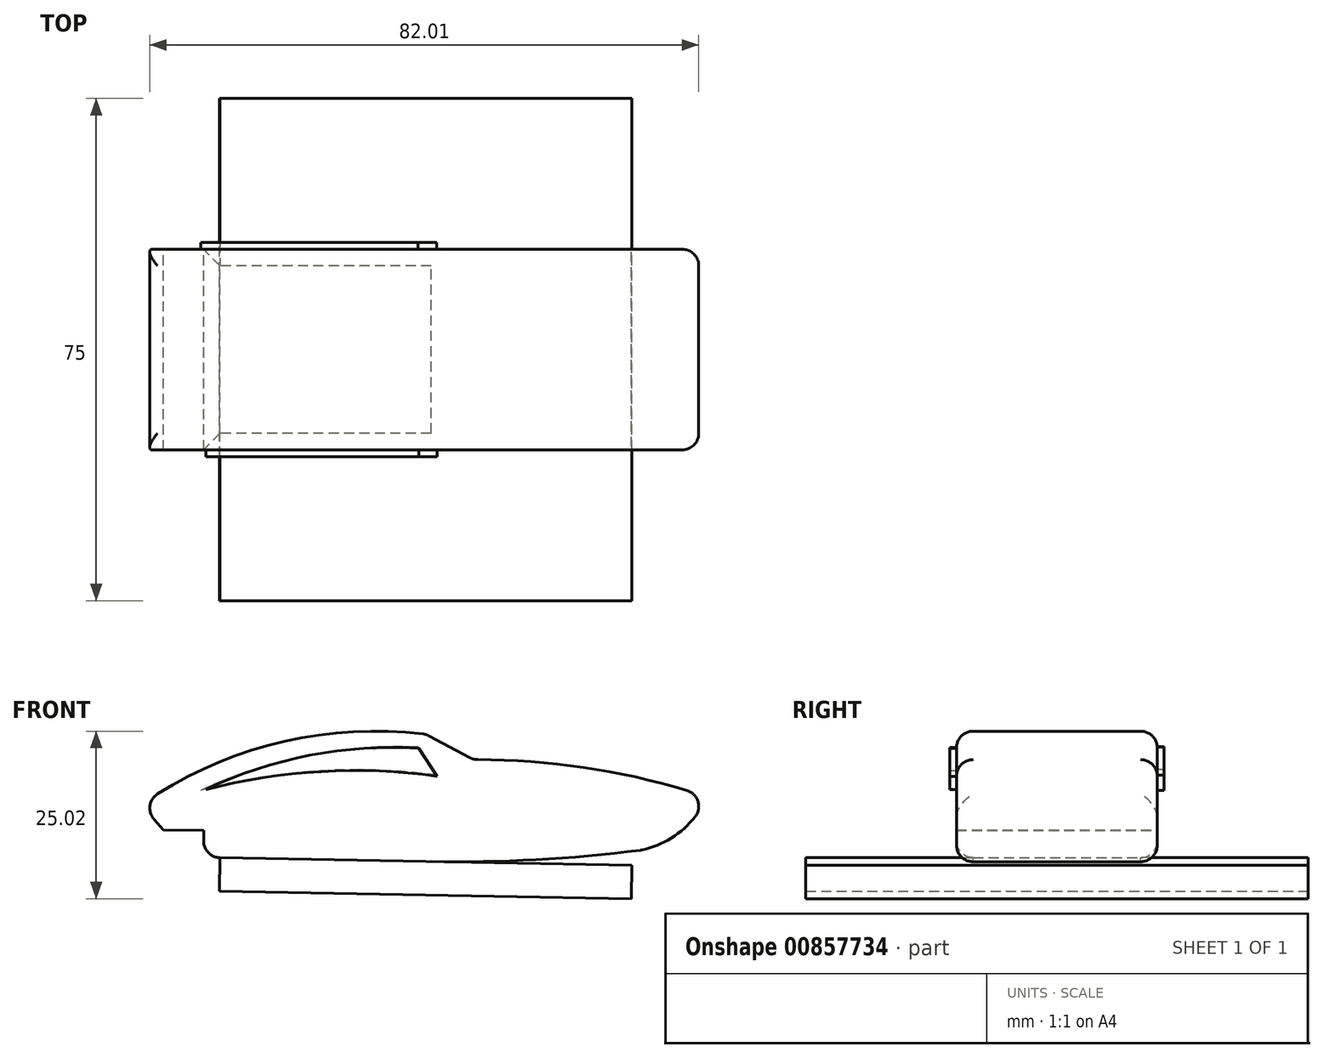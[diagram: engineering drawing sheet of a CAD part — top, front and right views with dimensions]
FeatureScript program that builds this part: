
annotation { "Feature Type Name" : "Feature", "Feature Type Description" : "" }
export const myFeature = defineFeature(function(context is Context, id is Id, definition is map)
    precondition{}
    {
        {
            var Q0;
            Q0=qCreatedBy(makeId("Front.planeOp"),FACE);
            var sketch = newSketch(context, id + "F0", { "sketchPlane" : qUnion([Q0])});
            skArc(sketch, "E0", {"start": v(7.02, 25.19) * mm, "mid": v(-15.24, 23.88) * mm, "end": v(-35.55, 14.66) * mm});
            skLineSegment(sketch, "E1", {"start": v(7.02, 25.19) * mm, "end": v(14.08, 21.41) * mm});
            skArc(sketch, "E2", {"start": v(49.01, 15.85) * mm, "mid": v(31.77, 20.05) * mm, "end": v(14.08, 21.41) * mm});
            skArc(sketch, "E3", {"start": v(39.11, 7.89) * mm, "mid": v(45.02, 10.68) * mm, "end": v(49.01, 15.85) * mm});
            skLineSegment(sketch, "E4", {"start": v(-26.24, 6.8) * mm, "end": v(-26.24, 10.8) * mm, "construction": true});
            skLineSegment(sketch, "E5", {"start": v(7.75, 6.19) * mm, "end": v(-26.24, 6.8) * mm});
            skLineSegment(sketch, "E6", {"start": v(-26.24, 10.8) * mm, "end": v(-26.24, 6.8) * mm});
            skLineSegment(sketch, "E7", {"start": v(-26.24, 10.8) * mm, "end": v(-32.24, 10.92) * mm});
            skLineSegment(sketch, "E8", {"start": v(-32.24, 10.92) * mm, "end": v(-35.55, 14.66) * mm});
            skArc(sketch, "E9", {"start": v(7.75, 6.19) * mm, "mid": v(23.46, 6.47) * mm, "end": v(39.11, 7.89) * mm});
            skSolve(sketch);
        }
        {
            var Q0;
            Q0 = qSketchRegion(id + "F0", true);
            extrude(context, id + "F1", {"entities" : qUnion([Q0]), "depth" : 30 * mm, "offsetDistance" : 25 * mm});
        }
        {
            var Q0;
            Q0=makeQuery(id+"F1.opExtrude","CAP_FACE",FACE,{"disambiguationData":[OSD([sQuery(id+"F0.wireOp",EDGE,"E0"),sQuery(id+"F0.wireOp",EDGE,"E1"),sQuery(id+"F0.wireOp",EDGE,"E2"),sQuery(id+"F0.wireOp",EDGE,"E3"),sQuery(id+"F0.wireOp",EDGE,"E5"),sQuery(id+"F0.wireOp",EDGE,"E6"),sQuery(id+"F0.wireOp",EDGE,"E7"),sQuery(id+"F0.wireOp",EDGE,"E8"),sQuery(id+"F0.wireOp",EDGE,"E9")])],"isStart":false});
            var sketch = newSketch(context, id + "F2", { "sketchPlane" : qUnion([Q0])});
            skArc(sketch, "E10", {"start": v(5.94, 23.12) * mm, "mid": v(-10.37, 22.05) * mm, "end": v(-25.9, 16.94) * mm});
            skLineSegment(sketch, "E11", {"start": v(5.94, 23.12) * mm, "end": v(8.67, 18.92) * mm});
            skArc(sketch, "E12", {"start": v(8.67, 18.92) * mm, "mid": v(-8.72, 19.63) * mm, "end": v(-25.9, 16.94) * mm});
            skSolve(sketch);
        }
        {
            var Q0;
            Q0=makeQuery(id+"F1.opExtrude","CAP_FACE",FACE,{"disambiguationData":[OSD([sQuery(id+"F0.wireOp",EDGE,"E0"),sQuery(id+"F0.wireOp",EDGE,"E1"),sQuery(id+"F0.wireOp",EDGE,"E2"),sQuery(id+"F0.wireOp",EDGE,"E3"),sQuery(id+"F0.wireOp",EDGE,"E5"),sQuery(id+"F0.wireOp",EDGE,"E6"),sQuery(id+"F0.wireOp",EDGE,"E7"),sQuery(id+"F0.wireOp",EDGE,"E8"),sQuery(id+"F0.wireOp",EDGE,"E9")])],"isStart":true});
            var sketch = newSketch(context, id + "F3", { "sketchPlane" : qUnion([Q0])});
            skLineSegment(sketch, "E13", {"start": v(-8.59, 19.1) * mm, "end": v(-5.81, 23.26) * mm});
            skArc(sketch, "E14", {"start": v(26.65, 16.82) * mm, "mid": v(10.8, 21.99) * mm, "end": v(-5.81, 23.26) * mm});
            skArc(sketch, "E15", {"start": v(26.65, 16.82) * mm, "mid": v(9.14, 19.7) * mm, "end": v(-8.59, 19.1) * mm});
            skSolve(sketch);
        }
        {
            var Q0;
            Q0=makeQuery(id+"F2.imprint","IMPRINT",FACE,{"disambiguationData":[TD([[makeQuery(id+"F2.imprint","IMPRINT",EDGE,{"derivedFrom":sQuery(id+"F2.wireOp",EDGE,"E10")}),1.0]])]});
            extrude(context, id + "F4", {"entities" : qUnion([Q0]), "operationType" : NewBodyOperationType.ADD, "depth" : 1 * mm, "offsetDistance" : 25 * mm});
        }
        {
            var Q0;
            Q0=makeQuery(id+"F3.imprint","IMPRINT",FACE,{"disambiguationData":[TD([[makeQuery(id+"F3.imprint","IMPRINT",EDGE,{"derivedFrom":sQuery(id+"F3.wireOp",EDGE,"E13")}),-1.0]])]});
            extrude(context, id + "F5", {"entities" : qUnion([Q0]), "operationType" : NewBodyOperationType.ADD, "depth" : 1 * mm, "offsetDistance" : 25 * mm});
        }
        {
            var Q0;
            Q0=makeQuery(id+"F1.opExtrude","SWEPT_FACE",FACE,{"disambiguationData":[OSD([sQuery(id+"F0.wireOp",EDGE,"E2")])]});
            var Q1;
            Q1=makeQuery(id+"F1.opExtrude","SWEPT_FACE",FACE,{"disambiguationData":[OSD([sQuery(id+"F0.wireOp",EDGE,"E1")])]});
            var Q2;
            Q2=makeQuery(id+"F1.opExtrude","SWEPT_FACE",FACE,{"disambiguationData":[OSD([sQuery(id+"F0.wireOp",EDGE,"E0")])]});
            var Q3;
            Q3=makeQuery(id+"F1.opExtrude","SWEPT_FACE",FACE,{"disambiguationData":[OSD([sQuery(id+"F0.wireOp",EDGE,"E3")])]});
            var Q4;
            Q4=makeQuery(id+"F1.opExtrude","SWEPT_FACE",FACE,{"disambiguationData":[OSD([sQuery(id+"F0.wireOp",EDGE,"E9")])]});
            var Q5;
            Q5=makeQuery(id+"F1.opExtrude","SWEPT_FACE",FACE,{"disambiguationData":[OSD([sQuery(id+"F0.wireOp",EDGE,"E5")])]});
            fillet(context, id + "F6", {"entities" : qUnion([Q0, Q1, Q2, Q3, Q4, Q5]), "radius" : 2.5 * mm, "tangentPropagation" : true, "allowEdgeOverflow" : false});
        }
        {
            var Q0;
            Q0=makeQuery(id+"F1.opExtrude","SWEPT_FACE",FACE,{"disambiguationData":[OSD([sQuery(id+"F0.wireOp",EDGE,"E5")])]});
            extrude(context, id + "F7", {"entities" : qUnion([Q0]), "operationType" : NewBodyOperationType.ADD, "depth" : 5 * mm, "offsetDistance" : 25 * mm});
        }
        {
            var Q0;
            Q0=makeQuery(id+"F7.opExtrude","SWEPT_FACE",FACE,{"disambiguationData":[OSD([sQuery(id+"F0.wireOp",EDGE,"E5"),sQuery(id+"F0.wireOp",EDGE,"E9")])]});
            extrude(context, id + "F8", {"entities" : qUnion([Q0]), "operationType" : NewBodyOperationType.ADD, "depth" : 30 * mm, "offsetDistance" : 25 * mm});
        }
        {
            var Q0;
            {var subQ0=sQuery(id+"F0.wireOp",EDGE,"E9");var subQ1=sQuery(id+"F0.wireOp",EDGE,"E5");var subQ2=makeQuery(id+"F1.opExtrude","SWEPT_FACE",FACE,{"disambiguationData":[OSD([subQ1])]});var subQ3=makeQuery(id+"F1.opExtrude","CAP_EDGE",EDGE,{"disambiguationData":[OSD([subQ1])],"isStart":true});Q0=makeQuery(id+"F8.boolean.opBoolean","MERGE",FACE,{"derivedFrom":[makeQuery(id+"F7.opExtrude","SWEPT_FACE",FACE,{"disambiguationData":[OSD([subQ1]),TDD([makeQuery(id+"F6.opFillet","BLEND_EDGE",EDGE,{"blendedFrom":[subQ3,subQ2],"blendedInto":[subQ2]})])]}),makeQuery(id+"F8.opExtrude","SWEPT_FACE",FACE,{"disambiguationData":[OSD([subQ1,subQ0]),TDD([makeQuery(id+"F7.opExtrude","SWEPT_EDGE",EDGE,{"disambiguationData":[OSD([subQ1,subQ0]),TDD([makeQuery(id+"F6.opFillet","BLEND_VERTEX",VERTEX,{"blendedFrom":[subQ3,makeQuery(id+"F1.opExtrude","CAP_EDGE",EDGE,{"disambiguationData":[OSD([subQ0])],"isStart":true}),subQ2,makeQuery(id+"F1.opExtrude","SWEPT_FACE",FACE,{"disambiguationData":[OSD([subQ0])]})],"blendedInto":[subQ2,makeQuery(id+"F1.opExtrude","SWEPT_FACE",FACE,{"disambiguationData":[OSD([subQ0])]})]})])]})])]})]});}
            extrude(context, id + "F9", {"entities" : qUnion([Q0]), "operationType" : NewBodyOperationType.ADD, "depth" : 25 * mm, "offsetDistance" : 25 * mm});
        }
        {
            var Q0;
            {var subQ0=sQuery(id+"F0.wireOp",EDGE,"E9");var subQ1=sQuery(id+"F0.wireOp",EDGE,"E5");var subQ2=makeQuery(id+"F1.opExtrude","SWEPT_FACE",FACE,{"disambiguationData":[OSD([subQ1])]});var subQ3=makeQuery(id+"F1.opExtrude","CAP_EDGE",EDGE,{"disambiguationData":[OSD([subQ1])],"isStart":false});Q0=makeQuery(id+"F8.boolean.opBoolean","MERGE",FACE,{"derivedFrom":[makeQuery(id+"F7.opExtrude","SWEPT_FACE",FACE,{"disambiguationData":[OSD([subQ1]),TDD([makeQuery(id+"F6.opFillet","BLEND_EDGE",EDGE,{"blendedFrom":[subQ3,subQ2],"blendedInto":[subQ2]})])]}),makeQuery(id+"F8.opExtrude","SWEPT_FACE",FACE,{"disambiguationData":[OSD([subQ1,subQ0]),TDD([makeQuery(id+"F7.opExtrude","SWEPT_EDGE",EDGE,{"disambiguationData":[OSD([subQ1,subQ0]),TDD([makeQuery(id+"F6.opFillet","BLEND_VERTEX",VERTEX,{"blendedFrom":[subQ3,makeQuery(id+"F1.opExtrude","CAP_EDGE",EDGE,{"disambiguationData":[OSD([subQ0])],"isStart":false}),subQ2,makeQuery(id+"F1.opExtrude","SWEPT_FACE",FACE,{"disambiguationData":[OSD([subQ0])]})],"blendedInto":[subQ2,makeQuery(id+"F1.opExtrude","SWEPT_FACE",FACE,{"disambiguationData":[OSD([subQ0])]})]})])]})])]})]});}
            extrude(context, id + "F10", {"entities" : qUnion([Q0]), "operationType" : NewBodyOperationType.ADD, "depth" : 25 * mm, "offsetDistance" : 25 * mm});
        }
    });
